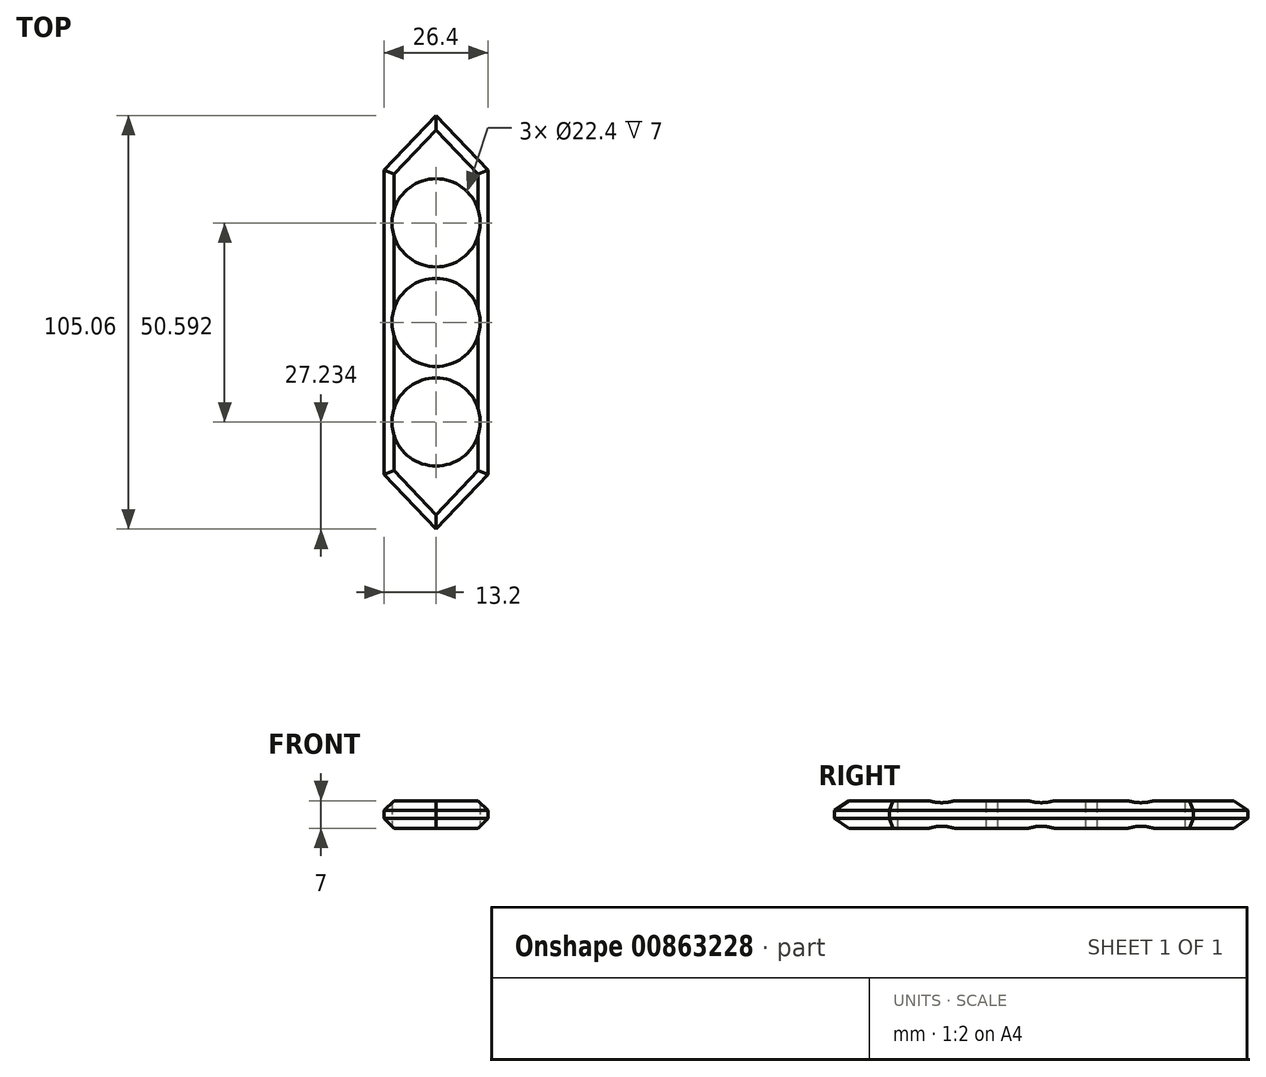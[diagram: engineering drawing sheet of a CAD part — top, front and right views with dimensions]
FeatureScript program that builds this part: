
annotation { "Feature Type Name" : "Feature", "Feature Type Description" : "" }
export const myFeature = defineFeature(function(context is Context, id is Id, definition is map)
    precondition{}
    {
        {
            var Q0;
            Q0=qCreatedBy(makeId("Top.planeOp"),FACE);
            var sketch = newSketch(context, id + "F0", { "sketchPlane" : qUnion([Q0])});
            skCircle(sketch, "E0", {"center": v(0, 0) * mm, "radius": 11.2 * mm});
            skCircle(sketch, "E1", {"center": v(0, 0) * mm, "radius": 13.2 * mm});
            skLineSegment(sketch, "E2", {"start": v(-13.2, 0) * mm, "end": v(-13.2, 38.64) * mm});
            skLineSegment(sketch, "E3", {"start": v(13.2, 0) * mm, "end": v(13.2, 38.64) * mm});
            skLineSegment(sketch, "E4", {"start": v(-13.2, 38.64) * mm, "end": v(0, 52.53) * mm});
            skLineSegment(sketch, "E5", {"start": v(0, 52.53) * mm, "end": v(13.2, 38.64) * mm});
            skLineSegment(sketch, "E6.1.0", {"start": v(0, -52.53) * mm, "end": v(-13.2, -38.64) * mm});
            skLineSegment(sketch, "E6.1.1", {"start": v(13.2, -38.64) * mm, "end": v(0, -52.53) * mm});
            skLineSegment(sketch, "E6.1.2", {"start": v(13.2, 0) * mm, "end": v(13.2, -38.64) * mm});
            skLineSegment(sketch, "E6.1.3", {"start": v(-13.2, 0) * mm, "end": v(-13.2, -38.64) * mm});
            skCircle(sketch, "E7", {"center": v(0, -25.3) * mm, "radius": 11.2 * mm});
            skCircle(sketch, "E8.1.0", {"center": v(0, 25.3) * mm, "radius": 11.2 * mm});
            skSolve(sketch);
        }
        {
            var Q0;
            {var subQ1=sQuery(id+"F0.wireOp",EDGE,"E2");Q0=makeQuery(id+"F0.imprint","IMPRINT",FACE,{"disambiguationData":[TD([[makeQuery(id+"F0.imprint","IMPRINT",EDGE,{"derivedFrom":subQ1}),-1.0]])]});}
            var Q1;
            Q1=makeQuery(id+"F0.imprint","IMPRINT",FACE,{"disambiguationData":[TD([[makeQuery(id+"F0.imprint","IMPRINT",EDGE,{"derivedFrom":sQuery(id+"F0.wireOp",EDGE,"E6.1.0")}),-1.0]])]});
            var Q2;
            Q2=makeQuery(id+"F0.imprint","IMPRINT",FACE,{"disambiguationData":[TD([[makeQuery(id+"F0.imprint","IMPRINT",EDGE,{"derivedFrom":sQuery(id+"F0.wireOp",EDGE,"E0")}),-1.0]])]});
            extrude(context, id + "F1", {"entities" : qUnion([Q0, Q1, Q2]), "depth" : 7 * mm, "offsetDistance" : 25 * mm});
        }
        {
            var Q0;
            Q0=makeQuery(id+"F1.opExtrude","CAP_EDGE",EDGE,{"disambiguationData":[OSD([sQuery(id+"F0.wireOp",EDGE,"E6.1.1")])],"isStart":false});
            var Q1;
            Q1=makeQuery(id+"F1.opExtrude","CAP_EDGE",EDGE,{"disambiguationData":[OSD([sQuery(id+"F0.wireOp",EDGE,"E6.1.0")])],"isStart":false});
            var Q2;
            Q2=makeQuery(id+"F1.opExtrude","CAP_EDGE",EDGE,{"disambiguationData":[OSD([sQuery(id+"F0.wireOp",EDGE,"E3"),sQuery(id+"F0.wireOp",EDGE,"E6.1.2")])],"isStart":false});
            var Q3;
            Q3=makeQuery(id+"F1.opExtrude","CAP_EDGE",EDGE,{"disambiguationData":[OSD([sQuery(id+"F0.wireOp",EDGE,"E2"),sQuery(id+"F0.wireOp",EDGE,"E6.1.3")])],"isStart":false});
            var Q4;
            Q4=makeQuery(id+"F1.opExtrude","CAP_EDGE",EDGE,{"disambiguationData":[OSD([sQuery(id+"F0.wireOp",EDGE,"E4")])],"isStart":false});
            var Q5;
            Q5=makeQuery(id+"F1.opExtrude","CAP_EDGE",EDGE,{"disambiguationData":[OSD([sQuery(id+"F0.wireOp",EDGE,"E5")])],"isStart":false});
            chamfer(context, id + "F2", {"entities" : qUnion([Q0, Q1, Q2, Q3, Q4, Q5]), "width" : 2.5 * mm, "tangentPropagation" : true});
        }
        {
            var Q0;
            Q0=makeQuery(id+"F1.opExtrude","CAP_EDGE",EDGE,{"disambiguationData":[OSD([sQuery(id+"F0.wireOp",EDGE,"E6.1.0")])],"isStart":true});
            var Q1;
            Q1=makeQuery(id+"F1.opExtrude","CAP_EDGE",EDGE,{"disambiguationData":[OSD([sQuery(id+"F0.wireOp",EDGE,"E6.1.1")])],"isStart":true});
            var Q2;
            Q2=makeQuery(id+"F1.opExtrude","CAP_EDGE",EDGE,{"disambiguationData":[OSD([sQuery(id+"F0.wireOp",EDGE,"E3"),sQuery(id+"F0.wireOp",EDGE,"E6.1.2")])],"isStart":true});
            var Q3;
            Q3=makeQuery(id+"F1.opExtrude","CAP_EDGE",EDGE,{"disambiguationData":[OSD([sQuery(id+"F0.wireOp",EDGE,"E2"),sQuery(id+"F0.wireOp",EDGE,"E6.1.3")])],"isStart":true});
            var Q4;
            Q4=makeQuery(id+"F1.opExtrude","CAP_EDGE",EDGE,{"disambiguationData":[OSD([sQuery(id+"F0.wireOp",EDGE,"E4")])],"isStart":true});
            var Q5;
            Q5=makeQuery(id+"F1.opExtrude","CAP_EDGE",EDGE,{"disambiguationData":[OSD([sQuery(id+"F0.wireOp",EDGE,"E5")])],"isStart":true});
            chamfer(context, id + "F3", {"entities" : qUnion([Q0, Q1, Q2, Q3, Q4, Q5]), "width" : 2.5 * mm, "tangentPropagation" : true});
        }
    });
